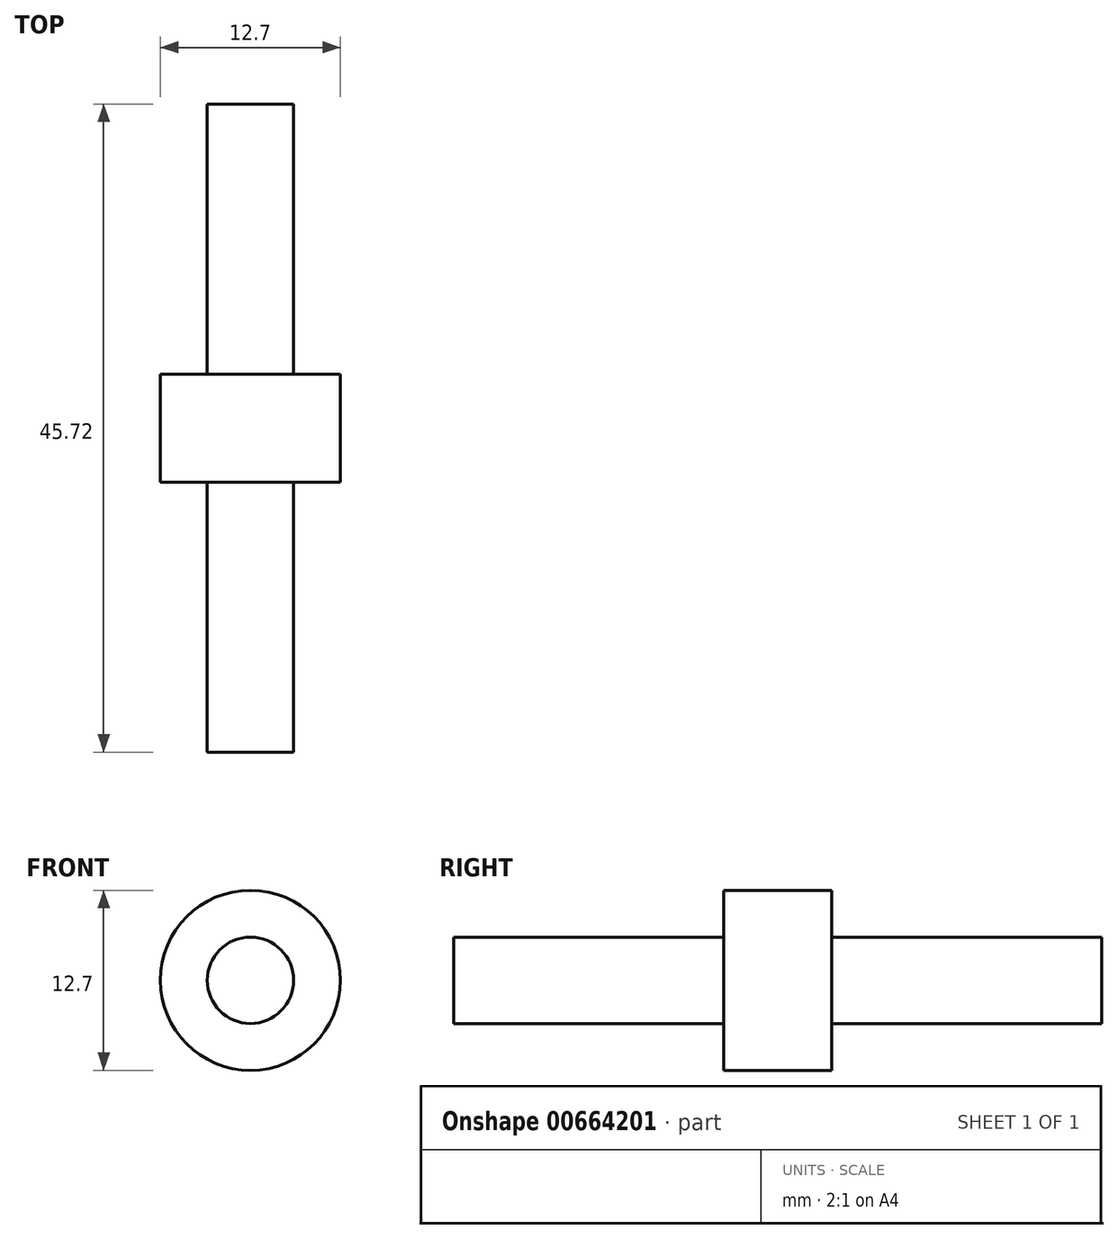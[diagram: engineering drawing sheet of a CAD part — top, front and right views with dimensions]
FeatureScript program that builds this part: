
annotation { "Feature Type Name" : "Feature", "Feature Type Description" : "" }
export const myFeature = defineFeature(function(context is Context, id is Id, definition is map)
    precondition{}
    {
        {
            var Q0;
            Q0=qCreatedBy(makeId("Front.planeOp"),FACE);
            var sketch = newSketch(context, id + "F0", { "sketchPlane" : qUnion([Q0])});
            skCircle(sketch, "E0", {"center": v(0, 0) * mm, "radius": 6.35 * mm});
            skSolve(sketch);
        }
        {
            var Q0;
            Q0 = qSketchRegion(id + "F0", true);
            extrude(context, id + "F1", {"entities" : qUnion([Q0]), "depth" : 7.62 * mm, "offsetDistance" : 25.4 * mm});
        }
        {
            var Q0;
            Q0=makeQuery(id+"F1.opExtrude","CAP_FACE",FACE,{"disambiguationData":[OSD([sQuery(id+"F0.wireOp",EDGE,"E0")])],"isStart":false});
            var sketch = newSketch(context, id + "F2", { "sketchPlane" : qUnion([Q0])});
            skCircle(sketch, "E1", {"center": v(0, 0) * mm, "radius": 3.05 * mm});
            skSolve(sketch);
        }
        {
            var Q0;
            Q0=makeQuery(id+"F2.imprint","IMPRINT",FACE,{"disambiguationData":[TD([[makeQuery(id+"F2.imprint","IMPRINT",EDGE,{"derivedFrom":sQuery(id+"F2.wireOp",EDGE,"E1")}),1.0]])]});
            extrude(context, id + "F3", {"entities" : qUnion([Q0]), "operationType" : NewBodyOperationType.ADD, "depth" : 19.05 * mm, "offsetDistance" : 25.4 * mm});
        }
        {
            var Q0;
            Q0=makeQuery(id+"F1.opExtrude","CAP_FACE",FACE,{"disambiguationData":[OSD([sQuery(id+"F0.wireOp",EDGE,"E0")])],"isStart":true});
            var sketch = newSketch(context, id + "F4", { "sketchPlane" : qUnion([Q0])});
            skCircle(sketch, "E2", {"center": v(0, 0) * mm, "radius": 3.05 * mm});
            skSolve(sketch);
        }
        {
            var Q0;
            Q0=makeQuery(id+"F4.imprint","IMPRINT",FACE,{"disambiguationData":[TD([[makeQuery(id+"F4.imprint","IMPRINT",EDGE,{"derivedFrom":sQuery(id+"F4.wireOp",EDGE,"E2")}),1.0]])]});
            extrude(context, id + "F5", {"entities" : qUnion([Q0]), "operationType" : NewBodyOperationType.ADD, "depth" : 19.05 * mm, "offsetDistance" : 25.4 * mm});
        }
    });
